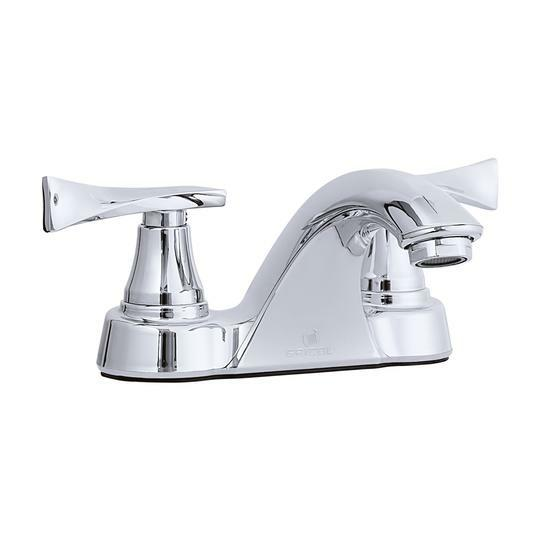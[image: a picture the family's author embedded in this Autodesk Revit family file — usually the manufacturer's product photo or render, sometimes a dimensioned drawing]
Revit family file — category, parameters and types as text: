
# Revit family: 01-2802-11 MEZCLADOR LAVAMANOS PLASTICO 4” PRISTINA
name_source: partatom
category: Plumbing Fixtures
revit_build: Autodesk Revit 2018 (Build: 20170223_1515(x64)
units: mm (PartAtom-declared; Revit-internal decimal feet)

## family parameters
Cut with Voids When Loaded = No
Host = Face
OmniClass Number = 23.31.11.00
Part Type = Normal
Room Calculation Point = No
Round Connector Dimension = Use Diameter
Shared = No

## types (1)
- 01-2802-11
    Aireador = 57.9 mm
    Ancho = 207.6 mm
    CW Connection = Yes
    Default Elevation = 0 mm  [stored 0 ft]
    Description = Bimando baño
    Eje (Rosca) = 101.64 mm  [stored 0.333465 ft]
    Eje-Aireador = 129.1 mm
    HW Connection = Yes
    Link ficha tecnica = https://infotecnica.gricol.com
    Manija = 75 mm
    Manufacturer = Gricol
    Model = 01-2802-11
    Plastico ABS Cromado = Plastico - ABS Cromado
    Product Name = MEZCLADOR LAVAMANOS PLASTICO 4” PRISTINA
    Type Image = MEZCLADOR LAVAMANOS PLASTICO 4” PRISTINA.jpg
    URL = https://www.gricol.com
    Vent Connection = No
    Waste Connection = No

note: [stored X ft] marks values corroborated as IEEE doubles in the binary element streams (Revit-internal decimal feet)

## geometry (parser evidence)
native form markers: Blend x2, Sweep x4
no freeform markers — native parametric forms only
